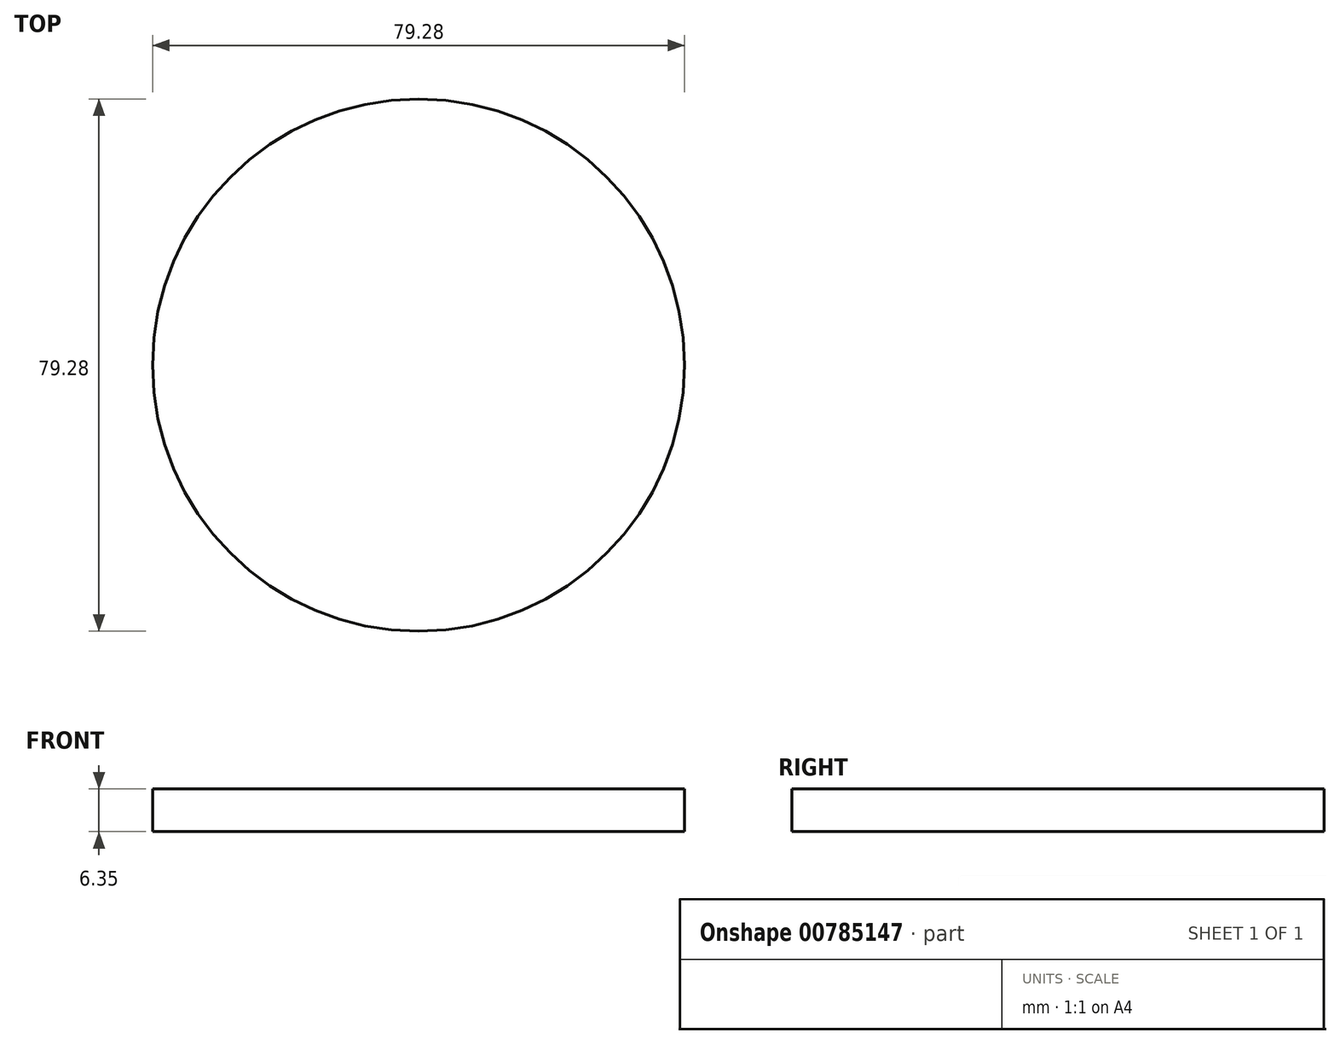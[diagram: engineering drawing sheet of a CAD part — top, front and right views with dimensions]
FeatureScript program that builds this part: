
annotation { "Feature Type Name" : "Feature", "Feature Type Description" : "" }
export const myFeature = defineFeature(function(context is Context, id is Id, definition is map)
    precondition{}
    {
        {
            var Q0;
            Q0=qCreatedBy(makeId("Top.planeOp"),FACE);
            var sketch = newSketch(context, id + "F0", { "sketchPlane" : qUnion([Q0])});
            skCircle(sketch, "E0", {"center": v(0, 0) * mm, "radius": 39.64 * mm});
            skSolve(sketch);
        }
        {
            var Q0;
            Q0 = qSketchRegion(id + "F0", true);
            extrude(context, id + "F1", {"entities" : qUnion([Q0]), "depth" : 6.35 * mm, "offsetDistance" : 25.4 * mm});
        }
    });
